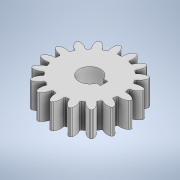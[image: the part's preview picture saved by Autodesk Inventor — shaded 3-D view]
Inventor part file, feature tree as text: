
AUTODESK INVENTOR PART (.ipt)
format: ipt  version: 2020 (Build 240168000, 168)  size: 322,560 bytes
history: native  units: mm
features: extrude x2, sketch x2, fillet x1, pattern_circular x1
ambient origin geometry x8: Origin, YZ Plane, XZ Plane, XY Plane, X Axis, Y Axis, Z Axis, Center Point
bodies: Solid1 (feature_tree)
feature tree (6):
  extrude  "Extrusion1"  Depth=7.0mm TaperAngle=360.0deg
  fillet  "Fillet2"  Radius=21.0mm
  pattern_circular  "Circular Pattern2"  [2 undecoded]
  extrude  "Extrusion6"  Depth=2.0mm
  sketch  "Sketch1"  dims[d4=7.0mm d5=0.0mm d18=170.0mm d19=360.0deg d23=21.0mm]
  sketch  "Sketch7"  dims[d25=1.544118mm d26=1.235294mm d27=3.490659mm d28=19.733545mm d29=3.490659mm d30=0.308824mm d31=0.617647mm d32=0.9702mm d33=0.4mm d87=6.0mm d88=2.0mm d89=2.0mm d90=2.0mm d91=0.0mm d92=0.0mm]
note: 2 required parameter values undecoded (feature->parameter linkage not recoverable at this tier; creation-order binding heuristic only, values carry confidence <= 0.55)
